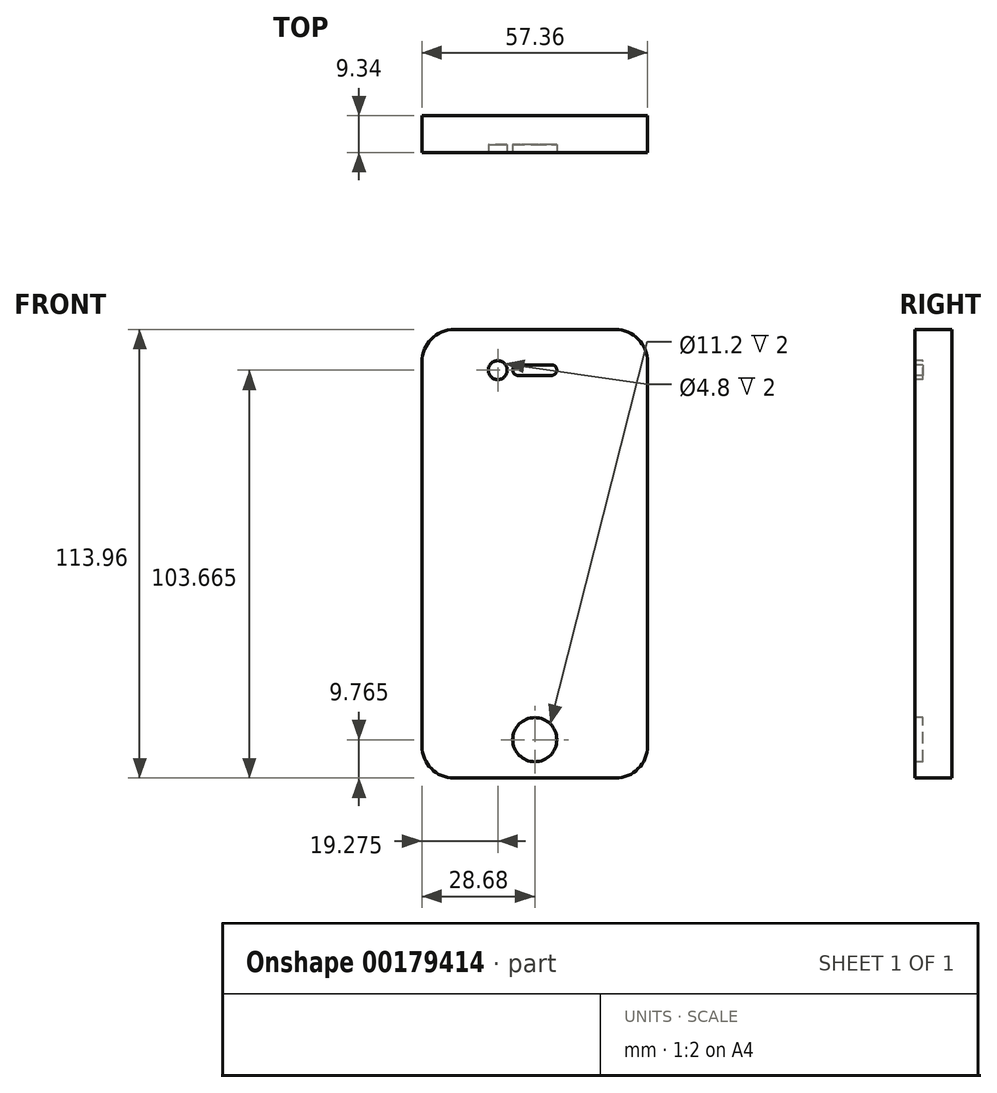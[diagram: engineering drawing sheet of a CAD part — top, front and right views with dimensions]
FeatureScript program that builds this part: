
annotation { "Feature Type Name" : "Feature", "Feature Type Description" : "" }
export const myFeature = defineFeature(function(context is Context, id is Id, definition is map)
    precondition{}
    {
        {
            var Q0;
            Q0=qCreatedBy(makeId("Front.planeOp"),FACE);
            var sketch = newSketch(context, id + "F0", { "sketchPlane" : qUnion([Q0])});
            skLineSegment(sketch, "E0.bottom", {"start": v(20.5, 56.97) * mm, "end": v(-20.5, 56.97) * mm});
            skLineSegment(sketch, "E0.top", {"start": v(20.5, -56.97) * mm, "end": v(-20.5, -56.97) * mm});
            skLineSegment(sketch, "E0.left", {"start": v(28.68, 48.8) * mm, "end": v(28.68, -48.8) * mm});
            skLineSegment(sketch, "E0.right", {"start": v(-28.68, 48.8) * mm, "end": v(-28.68, -48.8) * mm});
            skPoint(sketch, "E0.middle", {"position": v(0, 0) * mm});
            skPoint(sketch, "E1.visualSharp", {"position": v(-28.68, 56.97) * mm});
            skArc(sketch, "E1.filletArc", {"start": v(-20.5, 56.98) * mm, "mid": v(-26.28, 54.58) * mm, "end": v(-28.68, 48.8) * mm});
            skPoint(sketch, "E2.visualSharp", {"position": v(28.68, 56.97) * mm});
            skArc(sketch, "E2.filletArc", {"start": v(28.68, 48.8) * mm, "mid": v(26.28, 54.58) * mm, "end": v(20.5, 56.97) * mm});
            skPoint(sketch, "E3.visualSharp", {"position": v(28.68, -56.97) * mm});
            skArc(sketch, "E3.filletArc", {"start": v(20.5, -56.97) * mm, "mid": v(26.28, -54.58) * mm, "end": v(28.68, -48.8) * mm});
            skPoint(sketch, "E4.visualSharp", {"position": v(-28.68, -56.97) * mm});
            skArc(sketch, "E4.filletArc", {"start": v(-28.68, -48.8) * mm, "mid": v(-26.28, -54.58) * mm, "end": v(-20.5, -56.97) * mm});
            skSolve(sketch);
        }
        {
            var Q0;
            Q0 = qSketchRegion(id + "F0", true);
            extrude(context, id + "F1", {"entities" : qUnion([Q0]), "depth" : 9.34 * mm});
        }
        {
            var Q0;
            Q0=makeQuery(id+"F1.opExtrude","CAP_FACE",FACE,{"disambiguationData":[OSD([sQuery(id+"F0.wireOp",EDGE,"E0.bottom"),sQuery(id+"F0.wireOp",EDGE,"E0.top"),sQuery(id+"F0.wireOp",EDGE,"E0.left"),sQuery(id+"F0.wireOp",EDGE,"E0.right"),sQuery(id+"F0.wireOp",EDGE,"E1.filletArc"),sQuery(id+"F0.wireOp",EDGE,"E2.filletArc"),sQuery(id+"F0.wireOp",EDGE,"E3.filletArc"),sQuery(id+"F0.wireOp",EDGE,"E4.filletArc")])],"isStart":false});
            var sketch = newSketch(context, id + "F2", { "sketchPlane" : qUnion([Q0])});
            skLineSegment(sketch, "E5", {"start": v(0, 56.97) * mm, "end": v(0, -56.97) * mm, "construction": true});
            skLineSegment(sketch, "E6", {"start": v(-28.68, 46.68) * mm, "end": v(28.67, 46.69) * mm, "construction": true});
            skCircle(sketch, "E7", {"center": v(-9.4, 46.68) * mm, "radius": 2.4 * mm});
            skLineSegment(sketch, "E8.bottom", {"start": v(4.25, 45.34) * mm, "end": v(-4.25, 45.34) * mm});
            skLineSegment(sketch, "E8.top", {"start": v(4.25, 48.04) * mm, "end": v(-4.25, 48.04) * mm});
            skLineSegment(sketch, "E8.left", {"start": v(5.6, 46.68) * mm, "end": v(5.6, 46.69) * mm});
            skLineSegment(sketch, "E8.right", {"start": v(-5.6, 46.68) * mm, "end": v(-5.6, 46.69) * mm});
            skPoint(sketch, "E8.middle", {"position": v(0, 46.68) * mm});
            skPoint(sketch, "E9.visualSharp", {"position": v(-5.6, 48.04) * mm});
            skArc(sketch, "E9.filletArc", {"start": v(-4.25, 48.04) * mm, "mid": v(-5.2, 47.64) * mm, "end": v(-5.6, 46.69) * mm});
            skPoint(sketch, "E10.visualSharp", {"position": v(-5.6, 45.34) * mm});
            skArc(sketch, "E10.filletArc", {"start": v(-5.6, 46.68) * mm, "mid": v(-5.2, 45.73) * mm, "end": v(-4.25, 45.34) * mm});
            skPoint(sketch, "E11.visualSharp", {"position": v(5.6, 48.04) * mm});
            skArc(sketch, "E11.filletArc", {"start": v(5.6, 46.69) * mm, "mid": v(5.2, 47.64) * mm, "end": v(4.25, 48.03) * mm});
            skPoint(sketch, "E12.visualSharp", {"position": v(5.6, 45.34) * mm});
            skArc(sketch, "E12.filletArc", {"start": v(4.25, 45.34) * mm, "mid": v(5.2, 45.73) * mm, "end": v(5.6, 46.68) * mm});
            skCircle(sketch, "E13", {"center": v(0, -47.22) * mm, "radius": 5.6 * mm});
            skSolve(sketch);
        }
        {
            var Q0;
            Q0 = qSketchRegion(id + "F2", true);
            extrude(context, id + "F3", {"entities" : qUnion([Q0]), "operationType" : NewBodyOperationType.REMOVE, "oppositeDirection" : true, "depth" : 2 * mm});
        }
    });
